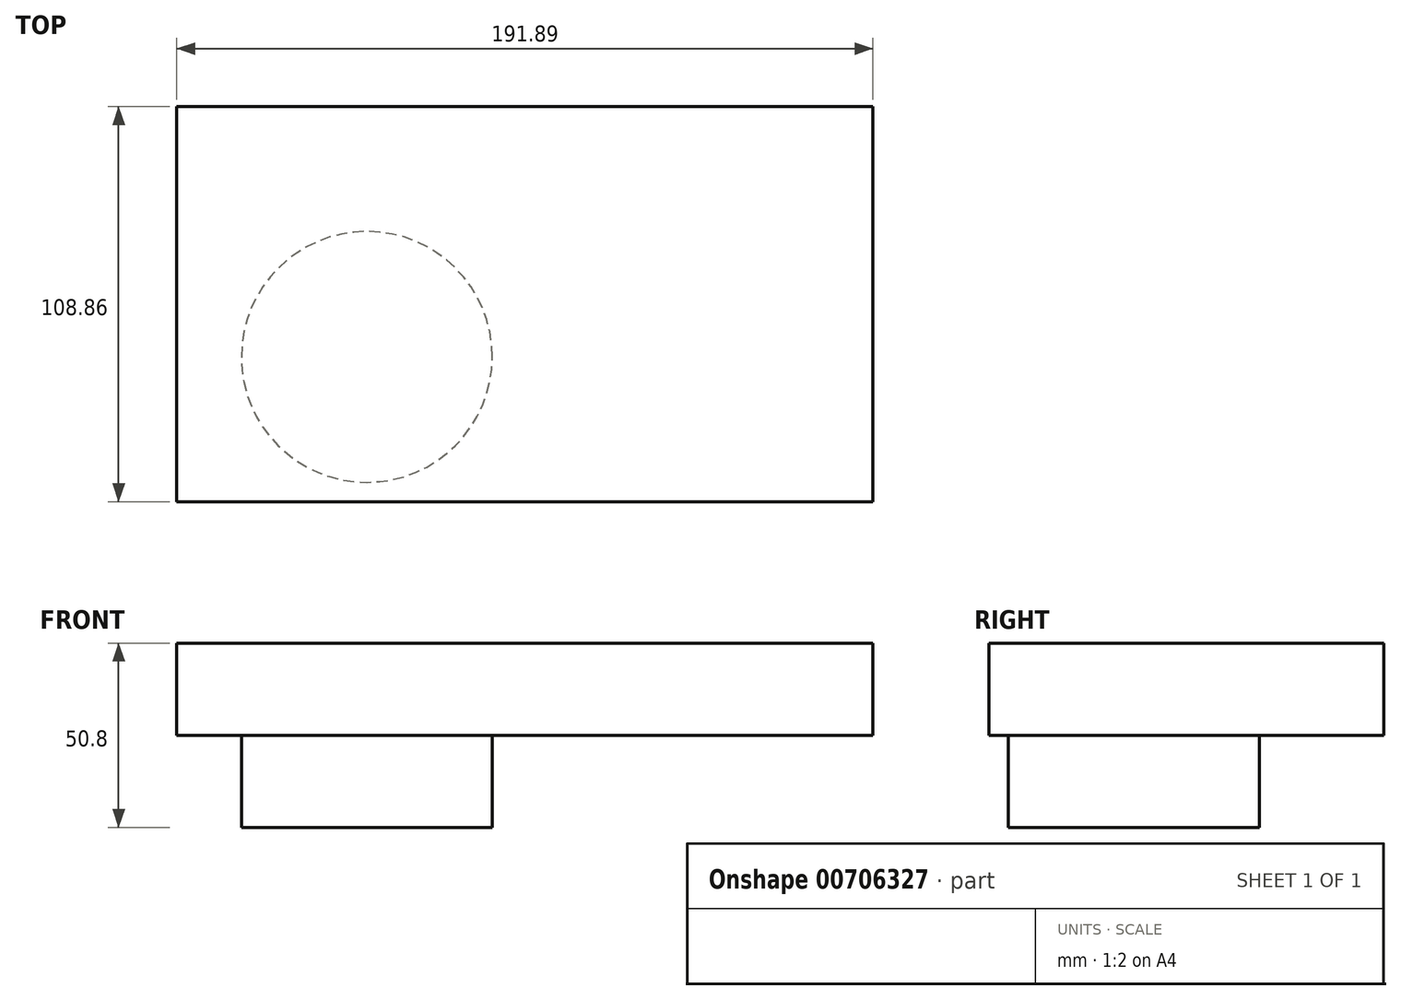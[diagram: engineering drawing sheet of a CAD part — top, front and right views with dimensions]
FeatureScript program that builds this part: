
annotation { "Feature Type Name" : "Feature", "Feature Type Description" : "" }
export const myFeature = defineFeature(function(context is Context, id is Id, definition is map)
    precondition{}
    {
        {
            var Q0;
            Q0=qCreatedBy(makeId("Top.planeOp"),FACE);
            var sketch = newSketch(context, id + "F0", { "sketchPlane" : qUnion([Q0])});
            skLineSegment(sketch, "E0.bottom", {"start": v(-96.97, 54.2) * mm, "end": v(94.92, 54.2) * mm});
            skLineSegment(sketch, "E0.top", {"start": v(-96.97, -54.66) * mm, "end": v(94.92, -54.66) * mm});
            skLineSegment(sketch, "E0.left", {"start": v(-96.97, 54.2) * mm, "end": v(-96.97, -54.66) * mm});
            skLineSegment(sketch, "E0.right", {"start": v(94.92, 54.2) * mm, "end": v(94.92, -54.66) * mm});
            skSolve(sketch);
        }
        {
            var Q0;
            Q0 = qSketchRegion(id + "F0", true);
            extrude(context, id + "F1", {"entities" : qUnion([Q0]), "depth" : 25.4 * mm, "offsetDistance" : 25.4 * mm});
        }
        {
            var Q0;
            Q0=makeQuery(id+"F1.opExtrude","CAP_FACE",FACE,{"disambiguationData":[OSD([sQuery(id+"F0.wireOp",EDGE,"E0.bottom"),sQuery(id+"F0.wireOp",EDGE,"E0.top"),sQuery(id+"F0.wireOp",EDGE,"E0.left"),sQuery(id+"F0.wireOp",EDGE,"E0.right")])],"isStart":true});
            var sketch = newSketch(context, id + "F2", { "sketchPlane" : qUnion([Q0])});
            skCircle(sketch, "E1", {"center": v(-44.6, 14.75) * mm, "radius": 34.57 * mm});
            skSolve(sketch);
        }
        {
            var Q0;
            Q0=makeQuery(id+"F2.imprint","IMPRINT",FACE,{"disambiguationData":[TD([[makeQuery(id+"F2.imprint","IMPRINT",EDGE,{"derivedFrom":sQuery(id+"F2.wireOp",EDGE,"E1")}),1.0]])]});
            extrude(context, id + "F3", {"entities" : qUnion([Q0]), "operationType" : NewBodyOperationType.ADD, "depth" : 25.4 * mm, "offsetDistance" : 25.4 * mm});
        }
    });
